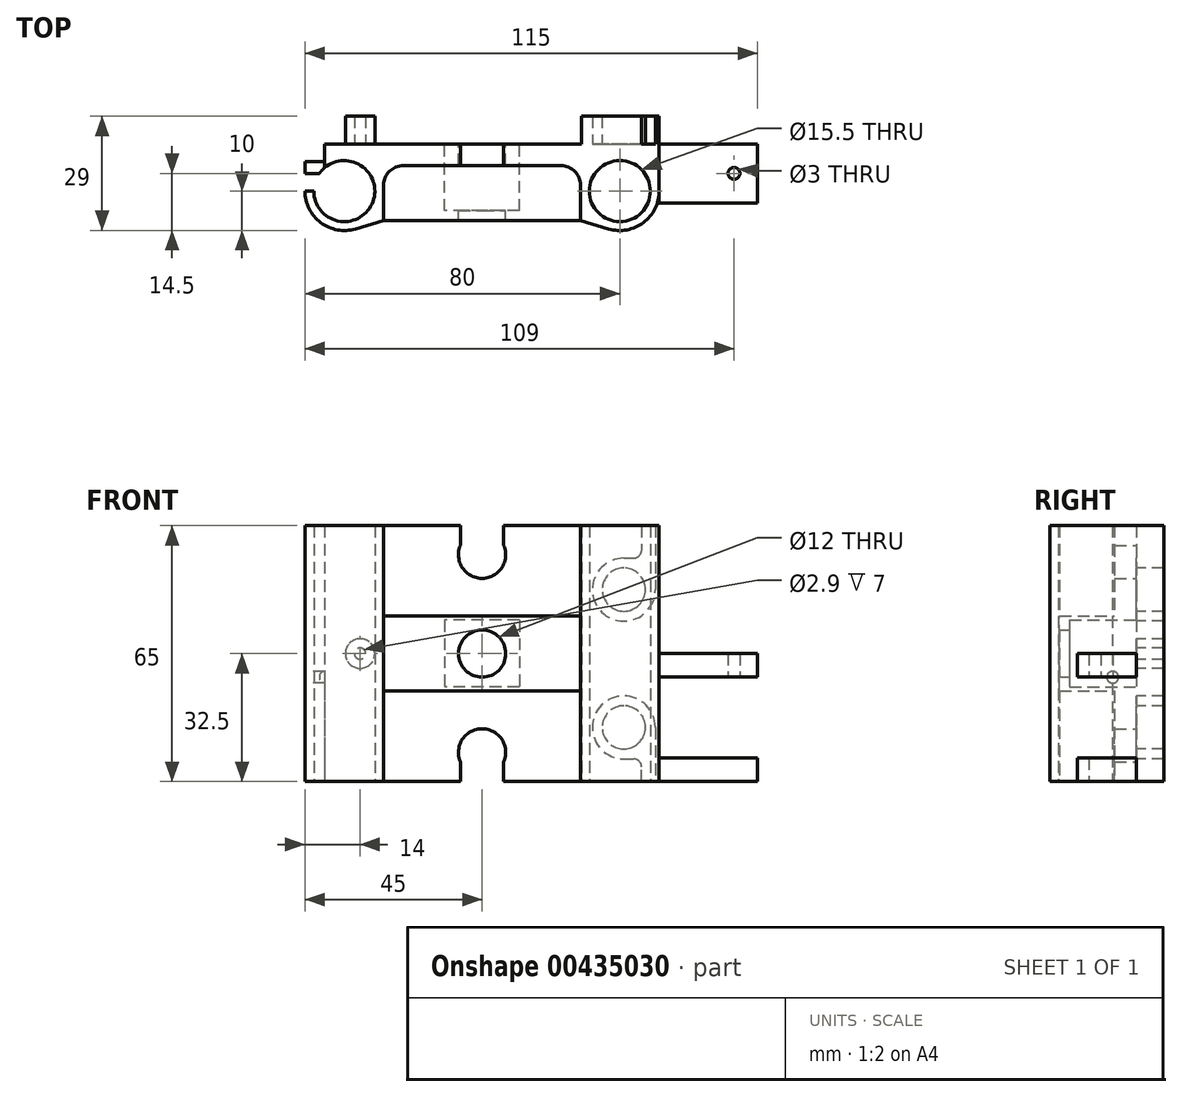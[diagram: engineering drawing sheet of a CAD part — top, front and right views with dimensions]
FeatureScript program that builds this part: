
annotation { "Feature Type Name" : "Feature", "Feature Type Description" : "" }
export const myFeature = defineFeature(function(context is Context, id is Id, definition is map)
    precondition{}
    {
        {
            var Q0;
            Q0=qCreatedBy(makeId("Top.planeOp"),FACE);
            var sketch = newSketch(context, id + "F0", { "sketchPlane" : qUnion([Q0])});
            skCircle(sketch, "E0", {"center": v(35, 0) * mm, "radius": 7.75 * mm});
            skArc(sketch, "E1", {"start": v(32.16, -9.59) * mm, "mid": v(40.98, -8.01) * mm, "end": v(45, 0) * mm});
            skLineSegment(sketch, "E2", {"start": v(45, 0) * mm, "end": v(45, 12) * mm});
            skLineSegment(sketch, "E3", {"start": v(45, 12) * mm, "end": v(0, 12) * mm});
            skLineSegment(sketch, "E4", {"start": v(25, 0) * mm, "end": v(25, 1.5) * mm});
            skPoint(sketch, "E5.visualSharp", {"position": v(25, 6.5) * mm});
            skArc(sketch, "E5.filletArc", {"start": v(25, 1.5) * mm, "mid": v(23.54, 5.04) * mm, "end": v(20, 6.5) * mm});
            skLineSegment(sketch, "E6.MirrorCS", {"start": v(-25, 0) * mm, "end": v(-25, 1.5) * mm});
            skCircle(sketch, "E7.MirrorC", {"center": v(-35, 0) * mm, "radius": 7.75 * mm});
            skArc(sketch, "E8.MirrorCS", {"start": v(-25, 1.5) * mm, "mid": v(-23.54, 5.04) * mm, "end": v(-20, 6.5) * mm});
            skPoint(sketch, "E9.MirrorP", {"position": v(-25, 6.5) * mm});
            skArc(sketch, "E10.MirrorC", {"start": v(-32.16, -9.59) * mm, "mid": v(-40.98, -8.01) * mm, "end": v(-45, 0) * mm});
            skLineSegment(sketch, "E11.MirrorCS", {"start": v(-45, 12) * mm, "end": v(0, 12) * mm});
            skLineSegment(sketch, "E12.MirrorCS", {"start": v(-45, 0) * mm, "end": v(-45, 12) * mm});
            skLineSegment(sketch, "E13", {"start": v(-20, 6.5) * mm, "end": v(20, 6.5) * mm});
            skLineSegment(sketch, "E14", {"start": v(25, 0) * mm, "end": v(25, -7.47) * mm});
            skLineSegment(sketch, "E15", {"start": v(25, -7.47) * mm, "end": v(35, -10.43) * mm});
            skPoint(sketch, "E15.endSnap0", {"position": v(35, -10) * mm});
            skLineSegment(sketch, "E16", {"start": v(35, -10.43) * mm, "end": v(35, -10) * mm});
            skLineSegment(sketch, "E17.MirrorCS", {"start": v(-25, 0) * mm, "end": v(-25, -7.47) * mm});
            skLineSegment(sketch, "E18.MirrorCS", {"start": v(-25, -7.47) * mm, "end": v(-35, -10.43) * mm});
            skSolve(sketch);
        }
        {
            var Q0;
            Q0=makeQuery(id+"F0.imprint","IMPRINT",FACE,{"disambiguationData":[TD([[makeQuery(id+"F0.imprint","IMPRINT",EDGE,{"derivedFrom":sQuery(id+"F0.wireOp",EDGE,"E0")}),-1.0]])]});
            extrude(context, id + "F1", {"entities" : qUnion([Q0]), "depth" : 65 * mm});
        }
        {
            var Q0;
            Q0=makeQuery(id+"F1.opExtrude","SWEPT_FACE",FACE,{"disambiguationData":[OSD([sQuery(id+"F0.wireOp",EDGE,"E3"),sQuery(id+"F0.wireOp",EDGE,"E11.MirrorCS")])]});
            var sketch = newSketch(context, id + "F2", { "sketchPlane" : qUnion([Q0])});
            skPoint(sketch, "E19.endSnap0", {"position": v(0, 0) * mm});
            skPoint(sketch, "E20.endSnap0", {"position": v(0, 65) * mm});
            skArc(sketch, "E21", {"start": v(-5.5, 60) * mm, "mid": v(0, 51.6) * mm, "end": v(5.5, 60) * mm});
            skArc(sketch, "E22", {"start": v(5.5, 5) * mm, "mid": v(0, 13.4) * mm, "end": v(-5.5, 5) * mm});
            skCircle(sketch, "E23", {"center": v(0, 32.5) * mm, "radius": 6 * mm});
            skLineSegment(sketch, "E24", {"start": v(-5.5, 65) * mm, "end": v(-5.5, 60) * mm});
            skLineSegment(sketch, "E25.MirrorCS", {"start": v(5.5, 65) * mm, "end": v(5.5, 60) * mm});
            skLineSegment(sketch, "E26", {"start": v(-5.5, 0) * mm, "end": v(-5.5, 5) * mm});
            skLineSegment(sketch, "E27.MirrorCS", {"start": v(5.5, 0) * mm, "end": v(5.5, 5) * mm});
            skLineSegment(sketch, "E28", {"start": v(5.5, 65) * mm, "end": v(-5.5, 65) * mm});
            skLineSegment(sketch, "E29", {"start": v(5.5, 0) * mm, "end": v(-5.5, 0) * mm});
            skLineSegment(sketch, "E30.bottom", {"start": v(-9.5, 41) * mm, "end": v(9.5, 41) * mm});
            skLineSegment(sketch, "E30.top", {"start": v(-9.5, 24) * mm, "end": v(9.5, 24) * mm});
            skLineSegment(sketch, "E30.left", {"start": v(-9.5, 41) * mm, "end": v(-9.5, 24) * mm});
            skLineSegment(sketch, "E30.right", {"start": v(9.5, 41) * mm, "end": v(9.5, 24) * mm});
            skLineSegment(sketch, "E31.bottom", {"start": v(-26.5, 23) * mm, "end": v(26.5, 23) * mm});
            skLineSegment(sketch, "E31.top", {"start": v(-26.5, 42) * mm, "end": v(26.5, 42) * mm});
            skLineSegment(sketch, "E31.left", {"start": v(-26.5, 23) * mm, "end": v(-26.5, 42) * mm});
            skLineSegment(sketch, "E31.right", {"start": v(26.5, 23) * mm, "end": v(26.5, 42) * mm});
            skSolve(sketch);
        }
        {
            var Q0;
            Q0=makeQuery(id+"F2.imprint","IMPRINT",FACE,{"disambiguationData":[TD([[makeQuery(id+"F2.imprint","IMPRINT",EDGE,{"derivedFrom":sQuery(id+"F2.wireOp",EDGE,"E21")}),1.0]])]});
            var Q1;
            Q1=makeQuery(id+"F2.imprint","IMPRINT",FACE,{"disambiguationData":[TD([[makeQuery(id+"F2.imprint","IMPRINT",EDGE,{"derivedFrom":sQuery(id+"F2.wireOp",EDGE,"E23")}),1.0]])]});
            var Q2;
            Q2=makeQuery(id+"F2.imprint","IMPRINT",FACE,{"disambiguationData":[TD([[makeQuery(id+"F2.imprint","IMPRINT",EDGE,{"derivedFrom":sQuery(id+"F2.wireOp",EDGE,"E22")}),1.0]])]});
            extrude(context, id + "F3", {"entities" : qUnion([Q0, Q1, Q2]), "operationType" : NewBodyOperationType.REMOVE, "oppositeDirection" : true, "depth" : 25 * mm});
        }
        {
            var Q0;
            Q0=makeQuery(id+"F1.opExtrude","SWEPT_FACE",FACE,{"disambiguationData":[OSD([sQuery(id+"F0.wireOp",EDGE,"E2")])]});
            var sketch = newSketch(context, id + "F4", { "sketchPlane" : qUnion([Q0])});
            skLineSegment(sketch, "E32.bottom", {"start": v(12, 32.5) * mm, "end": v(-3, 32.5) * mm});
            skLineSegment(sketch, "E32.top", {"start": v(12, 26.5) * mm, "end": v(-3, 26.5) * mm});
            skLineSegment(sketch, "E32.left", {"start": v(12, 32.5) * mm, "end": v(12, 26.5) * mm});
            skLineSegment(sketch, "E32.right", {"start": v(-3, 32.5) * mm, "end": v(-3, 26.5) * mm});
            skLineSegment(sketch, "E33.bottom", {"start": v(12, 0) * mm, "end": v(-3, 0) * mm});
            skLineSegment(sketch, "E33.top", {"start": v(12, 6) * mm, "end": v(-3, 6) * mm});
            skLineSegment(sketch, "E33.left", {"start": v(12, 0) * mm, "end": v(12, 6) * mm});
            skLineSegment(sketch, "E33.right", {"start": v(-3, 0) * mm, "end": v(-3, 6) * mm});
            skSolve(sketch);
        }
        {
            var Q0;
            Q0 = qSketchRegion(id + "F4", true);
            extrude(context, id + "F5", {"entities" : qUnion([Q0]), "operationType" : NewBodyOperationType.ADD, "depth" : 25 * mm});
        }
        {
            var Q0;
            Q0=makeQuery(id+"F5.opExtrude","SWEPT_FACE",FACE,{"disambiguationData":[OSD([sQuery(id+"F4.wireOp",EDGE,"E32.top")])]});
            var sketch = newSketch(context, id + "F6", { "sketchPlane" : qUnion([Q0])});
            skLineSegment(sketch, "E34", {"start": v(70, -4.5) * mm, "end": v(64, -4.5) * mm, "construction": true});
            skCircle(sketch, "E35", {"center": v(64, -4.5) * mm, "radius": 1.5 * mm});
            skSolve(sketch);
        }
        {
            var Q0;
            Q0=makeQuery(id+"F6.imprint","IMPRINT",FACE,{"disambiguationData":[TD([[makeQuery(id+"F6.imprint","IMPRINT",EDGE,{"derivedFrom":sQuery(id+"F6.wireOp",EDGE,"E35")}),1.0]])]});
            extrude(context, id + "F7", {"entities" : qUnion([Q0]), "operationType" : NewBodyOperationType.REMOVE, "oppositeDirection" : true, "depth" : 25 * mm});
        }
        {
            var Q0;
            Q0=makeQuery(id+"F5.boolean.opBoolean","MERGE",FACE,{"derivedFrom":[makeQuery(id+"F1.opExtrude","SWEPT_FACE",FACE,{"disambiguationData":[OSD([sQuery(id+"F0.wireOp",EDGE,"E3"),sQuery(id+"F0.wireOp",EDGE,"E11.MirrorCS")])]}),makeQuery(id+"F5.opExtrude","SWEPT_FACE",FACE,{"disambiguationData":[OSD([sQuery(id+"F4.wireOp",EDGE,"E32.left")])]}),makeQuery(id+"F5.opExtrude","SWEPT_FACE",FACE,{"disambiguationData":[OSD([sQuery(id+"F4.wireOp",EDGE,"E33.left")])]})]});
            var sketch = newSketch(context, id + "F8", { "sketchPlane" : qUnion([Q0])});
            skLineSegment(sketch, "E36", {"start": v(-45, 65) * mm, "end": v(-45, 0) * mm});
            skLineSegment(sketch, "E37", {"start": v(45, 65) * mm, "end": v(45, 0) * mm});
            skLineSegment(sketch, "E38", {"start": v(45, 32.5) * mm, "end": v(31, 32.5) * mm, "construction": true});
            skCircle(sketch, "E39", {"center": v(31, 32.5) * mm, "radius": 3.75 * mm});
            skLineSegment(sketch, "E40", {"start": v(-45, 65) * mm, "end": v(-44, 65) * mm});
            skLineSegment(sketch, "E41", {"start": v(-44, 65) * mm, "end": v(-44, 0) * mm});
            skPoint(sketch, "E42.startSnap0", {"position": v(-36, 13.75) * mm});
            skLineSegment(sketch, "E43", {"start": v(-44, 48.75) * mm, "end": v(-36, 48.75) * mm});
            skPoint(sketch, "E43.startSnap0", {"position": v(-45, 48.75) * mm});
            skCircle(sketch, "E44", {"center": v(-36, 13.75) * mm, "radius": 5.5 * mm});
            skCircle(sketch, "E45", {"center": v(-36, 48.75) * mm, "radius": 5.5 * mm});
            skLineSegment(sketch, "E46", {"start": v(-44, 0) * mm, "end": v(-40.5, 0) * mm});
            skLineSegment(sketch, "E47", {"start": v(-40.5, 0) * mm, "end": v(-40.5, 6) * mm});
            skLineSegment(sketch, "E48", {"start": v(-36, 54.25) * mm, "end": v(-36, 56.75) * mm, "construction": true});
            skLineSegment(sketch, "E49", {"start": v(-36, 8.25) * mm, "end": v(-36, 5.75) * mm, "construction": true});
            skLineSegment(sketch, "E50", {"start": v(-44, 65) * mm, "end": v(-40.5, 65) * mm});
            skLineSegment(sketch, "E51", {"start": v(-40.5, 65) * mm, "end": v(-40.5, 58.75) * mm});
            skLineSegment(sketch, "E52", {"start": v(-36, 5.75) * mm, "end": v(-38.5, 5.75) * mm});
            skLineSegment(sketch, "E53", {"start": v(-40.5, 6) * mm, "end": v(-40.5, 3.75) * mm});
            skLineSegment(sketch, "E54", {"start": v(-40.5, 65) * mm, "end": v(-40.5, 65) * mm});
            skPoint(sketch, "E55.visualSharp", {"position": v(-40.5, 5.75) * mm});
            skArc(sketch, "E55.filletArc", {"start": v(-38.5, 5.75) * mm, "mid": v(-39.91, 5.16) * mm, "end": v(-40.5, 3.75) * mm});
            skLineSegment(sketch, "E56", {"start": v(-36, 43.25) * mm, "end": v(-36, 40.75) * mm, "construction": true});
            skPoint(sketch, "E57.visualSharp", {"position": v(-28.5, 48.25) * mm});
            skArc(sketch, "E57.filletArc", {"start": v(-29.5, 47.37) * mm, "mid": v(-29.76, 48) * mm, "end": v(-30.38, 48.25) * mm});
            skArc(sketch, "E58", {"start": v(-44, 48.75) * mm, "mid": v(-30.34, 43.1) * mm, "end": v(-36, 56.75) * mm});
            skPoint(sketch, "E42.start.orphan", {"position": v(-44, 13.75) * mm});
            skArc(sketch, "E59", {"start": v(-36, 5.75) * mm, "mid": v(-30.34, 19.4) * mm, "end": v(-44, 13.75) * mm});
            skLineSegment(sketch, "E60", {"start": v(-45, 65) * mm, "end": v(-25.25, 65) * mm});
            skLineSegment(sketch, "E61", {"start": v(-25.25, 65) * mm, "end": v(-25.25, 0) * mm});
            skLineSegment(sketch, "E62", {"start": v(-45, 0) * mm, "end": v(-44, 0) * mm});
            skCircle(sketch, "E63", {"center": v(31, 32.5) * mm, "radius": 1.45 * mm});
            skLineSegment(sketch, "E64", {"start": v(-36, 56.75) * mm, "end": v(-38.5, 56.75) * mm});
            skPoint(sketch, "E65.visualSharp", {"position": v(-40.5, 56.75) * mm});
            skArc(sketch, "E65.filletArc", {"start": v(-40.5, 58.75) * mm, "mid": v(-39.91, 57.34) * mm, "end": v(-38.5, 56.75) * mm});
            skSolve(sketch);
        }
        {
            var Q0;
            Q0=makeQuery(id+"F8.imprint","IMPRINT",FACE,{"disambiguationData":[TD([[makeQuery(id+"F8.imprint","IMPRINT",EDGE,{"derivedFrom":sQuery(id+"F8.wireOp",EDGE,"E39")}),1.0]])]});
            var Q1;
            {var subQ6=sQuery(id+"F8.wireOp",EDGE,"E47");Q1=makeQuery(id+"F8.imprint","IMPRINT",FACE,{"disambiguationData":[TD([[makeQuery(id+"F8.imprint","IMPRINT",EDGE,{"derivedFrom":subQ6}),-1.0]])]});}
            var Q2;
            {var subQ8=sQuery(id+"F8.wireOp",EDGE,"E62");Q2=makeQuery(id+"F8.imprint","IMPRINT",FACE,{"disambiguationData":[TD([[makeQuery(id+"F8.imprint","IMPRINT",EDGE,{"derivedFrom":subQ8}),1.0]])]});}
            var Q3;
            Q3=makeQuery(id+"F8.imprint","IMPRINT",FACE,{"disambiguationData":[TD([[makeQuery(id+"F8.imprint","IMPRINT",EDGE,{"derivedFrom":sQuery(id+"F8.wireOp",EDGE,"E44")}),1.0]])]});
            var Q4;
            Q4=makeQuery(id+"F8.imprint","IMPRINT",FACE,{"disambiguationData":[TD([[makeQuery(id+"F8.imprint","IMPRINT",EDGE,{"derivedFrom":sQuery(id+"F8.wireOp",EDGE,"E45")}),1.0]])]});
            extrude(context, id + "F9", {"entities" : qUnion([Q0, Q1, Q2, Q3, Q4]), "operationType" : NewBodyOperationType.ADD, "depth" : 7 * mm});
        }
        {
            var Q0;
            Q0=makeQuery(id+"F1.opExtrude","SWEPT_FACE",FACE,{"disambiguationData":[OSD([sQuery(id+"F0.wireOp",EDGE,"E12.MirrorCS")])]});
            var sketch = newSketch(context, id + "F10", { "sketchPlane" : qUnion([Q0])});
            skLineSegment(sketch, "E66", {"start": v(-12, 32.5) * mm, "end": v(-6, 32.5) * mm, "construction": true});
            skLineSegment(sketch, "E67", {"start": v(-6, 32.5) * mm, "end": v(-6, 38.5) * mm, "construction": true});
            skCircle(sketch, "E68", {"center": v(-6, 38.5) * mm, "radius": 1.5 * mm});
            skCircle(sketch, "E69.MirrorC", {"center": v(-6, 26.5) * mm, "radius": 1.5 * mm});
            skSolve(sketch);
        }
        {
            var Q0;
            Q0=makeQuery(id+"F10.imprint","IMPRINT",FACE,{"disambiguationData":[TD([[makeQuery(id+"F10.imprint","IMPRINT",EDGE,{"derivedFrom":sQuery(id+"F10.wireOp",EDGE,"E69.MirrorC")}),-1.0]])]});
            var Q1;
            Q1=makeQuery(id+"F10.imprint","IMPRINT",FACE,{"disambiguationData":[TD([[makeQuery(id+"F10.imprint","IMPRINT",EDGE,{"derivedFrom":sQuery(id+"F10.wireOp",EDGE,"E68")}),1.0]])]});
            extrude(context, id + "F11", {"entities" : qUnion([Q0, Q1]), "operationType" : NewBodyOperationType.REMOVE, "oppositeDirection" : true, "depth" : 5 * mm});
        }
        {
            var Q0;
            Q0=makeQuery(id+"F2.imprint","IMPRINT",FACE,{"disambiguationData":[TD([[makeQuery(id+"F2.imprint","IMPRINT",EDGE,{"derivedFrom":sQuery(id+"F2.wireOp",EDGE,"E30.bottom")}),1.0]])]});
            var Q1;
            Q1=makeQuery(id+"F2.imprint","IMPRINT",FACE,{"disambiguationData":[TD([[makeQuery(id+"F2.imprint","IMPRINT",EDGE,{"derivedFrom":sQuery(id+"F2.wireOp",EDGE,"E23")}),-1.0]])]});
            extrude(context, id + "F12", {"entities" : qUnion([Q0, Q1]), "operationType" : NewBodyOperationType.ADD, "depth" : -19.47 * mm});
        }
        {
            var Q0;
            Q0=makeQuery(id+"F2.imprint","IMPRINT",FACE,{"disambiguationData":[TD([[makeQuery(id+"F2.imprint","IMPRINT",EDGE,{"derivedFrom":sQuery(id+"F2.wireOp",EDGE,"E23")}),-1.0]])]});
            extrude(context, id + "F13", {"entities" : qUnion([Q0]), "operationType" : NewBodyOperationType.REMOVE, "oppositeDirection" : true, "depth" : 17 * mm});
        }
    });
